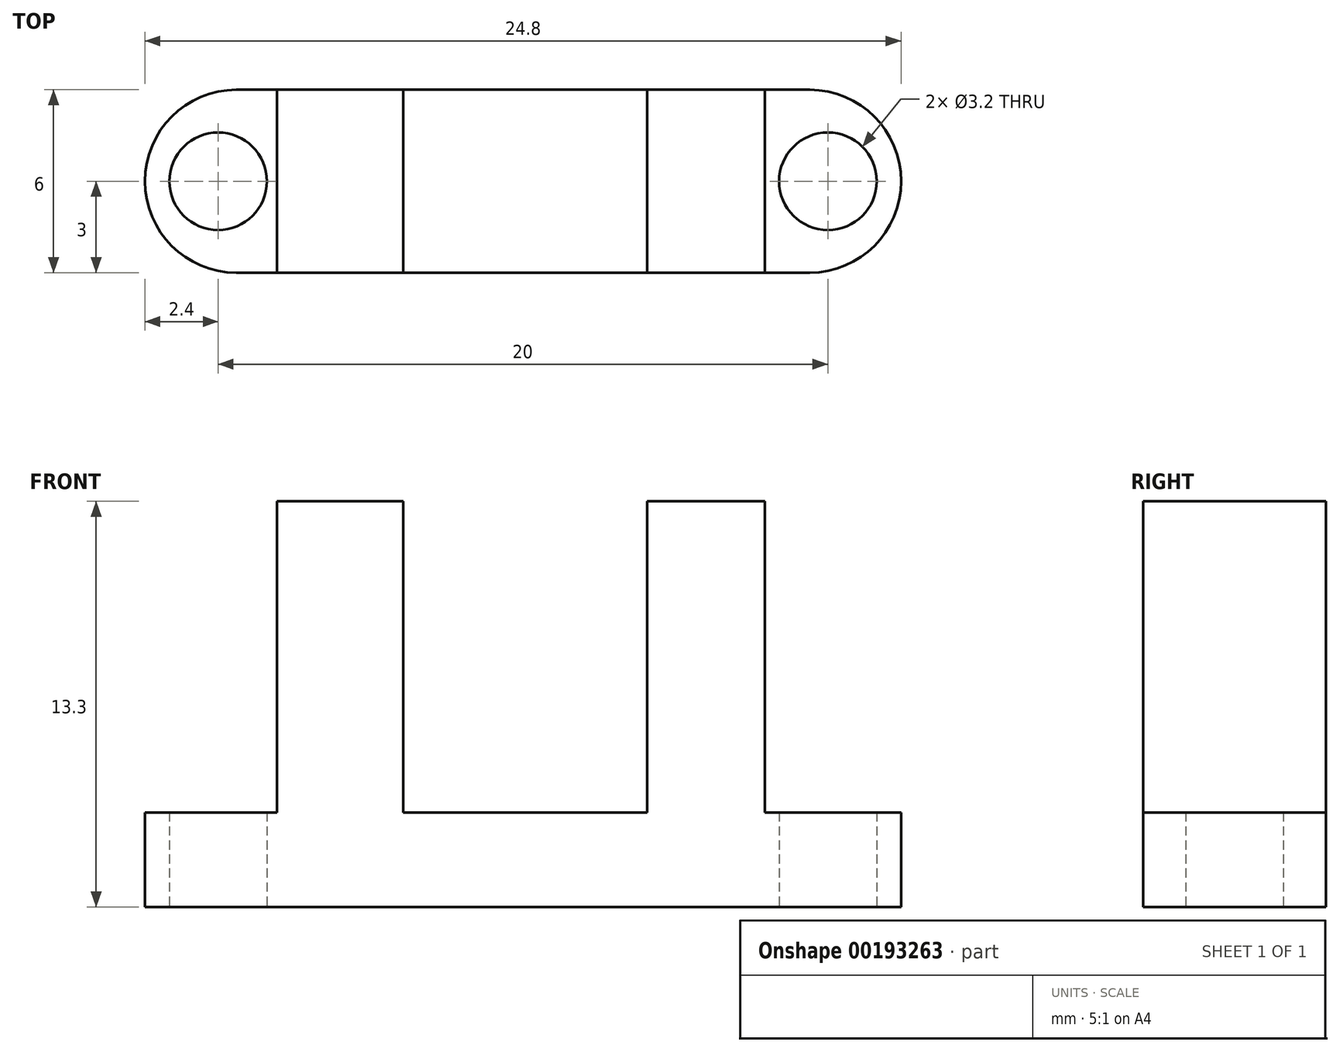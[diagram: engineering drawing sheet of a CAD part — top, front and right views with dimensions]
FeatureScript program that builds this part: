
annotation { "Feature Type Name" : "Feature", "Feature Type Description" : "" }
export const myFeature = defineFeature(function(context is Context, id is Id, definition is map)
    precondition{}
    {
        {
            var Q0;
            Q0=qCreatedBy(makeId("Top.planeOp"),FACE);
            var sketch = newSketch(context, id + "F0", { "sketchPlane" : qUnion([Q0])});
            skLineSegment(sketch, "E0.bottom", {"start": v(9.4, 3) * mm, "end": v(-9.4, 3) * mm});
            skLineSegment(sketch, "E0.top", {"start": v(9.4, -3) * mm, "end": v(-9.4, -3) * mm});
            skLineSegment(sketch, "E0.left", {"start": v(12.4, 0) * mm, "end": v(12.4, 0) * mm});
            skLineSegment(sketch, "E0.right", {"start": v(-12.4, 0) * mm, "end": v(-12.4, 0) * mm});
            skPoint(sketch, "E0.middle", {"position": v(0, 0) * mm});
            skLineSegment(sketch, "E1", {"start": v(0, 0) * mm, "end": v(10, 0) * mm});
            skCircle(sketch, "E2", {"center": v(10, 0) * mm, "radius": 1.6 * mm});
            skLineSegment(sketch, "E3", {"start": v(0, 0) * mm, "end": v(-10, 0) * mm});
            skCircle(sketch, "E4", {"center": v(-10, 0) * mm, "radius": 1.6 * mm});
            skPoint(sketch, "E5.visualSharp", {"position": v(-12.4, 3) * mm});
            skArc(sketch, "E5.filletArc", {"start": v(-9.4, 3) * mm, "mid": v(-11.52, 2.12) * mm, "end": v(-12.4, 0) * mm});
            skPoint(sketch, "E6.visualSharp", {"position": v(12.4, 3) * mm});
            skArc(sketch, "E6.filletArc", {"start": v(12.4, 0) * mm, "mid": v(11.52, 2.12) * mm, "end": v(9.4, 3) * mm});
            skPoint(sketch, "E7.visualSharp", {"position": v(-12.4, -3) * mm});
            skArc(sketch, "E7.filletArc", {"start": v(-12.4, 0) * mm, "mid": v(-11.52, -2.12) * mm, "end": v(-9.4, -3) * mm});
            skPoint(sketch, "E8.visualSharp", {"position": v(12.4, -3) * mm});
            skArc(sketch, "E8.filletArc", {"start": v(9.4, -3) * mm, "mid": v(11.52, -2.12) * mm, "end": v(12.4, 0) * mm});
            skSolve(sketch);
        }
        {
            var Q0;
            Q0 = qSketchRegion(id + "F0", true);
            extrude(context, id + "F1", {"entities" : qUnion([Q0]), "depth" : 3.1 * mm});
        }
        {
            var Q0;
            Q0=makeQuery(id+"F1.opExtrude","CAP_FACE",FACE,{"disambiguationData":[OSD([sQuery(id+"F0.wireOp",EDGE,"E0.bottom"),sQuery(id+"F0.wireOp",EDGE,"E0.top"),sQuery(id+"F0.wireOp",EDGE,"E0.left"),sQuery(id+"F0.wireOp",EDGE,"E0.right"),sQuery(id+"F0.wireOp",EDGE,"E2"),sQuery(id+"F0.wireOp",EDGE,"E4"),sQuery(id+"F0.wireOp",EDGE,"E5.filletArc"),sQuery(id+"F0.wireOp",EDGE,"E6.filletArc"),sQuery(id+"F0.wireOp",EDGE,"E7.filletArc"),sQuery(id+"F0.wireOp",EDGE,"E8.filletArc")])],"isStart":false});
            var sketch = newSketch(context, id + "F2", { "sketchPlane" : qUnion([Q0])});
            skLineSegment(sketch, "E9", {"start": v(0, 0) * mm, "end": v(6, 0) * mm});
            skLineSegment(sketch, "E10.bottom", {"start": v(7.93, 3) * mm, "end": v(4.07, 3) * mm});
            skLineSegment(sketch, "E10.top", {"start": v(7.93, -3) * mm, "end": v(4.07, -3) * mm});
            skLineSegment(sketch, "E10.left", {"start": v(7.93, 3) * mm, "end": v(7.93, -3) * mm});
            skLineSegment(sketch, "E10.right", {"start": v(4.07, 3) * mm, "end": v(4.07, -3) * mm});
            skPoint(sketch, "E10.middle", {"position": v(6, 0) * mm});
            skLineSegment(sketch, "E11", {"start": v(0, 0) * mm, "end": v(-6, 0) * mm});
            skLineSegment(sketch, "E12.bottom", {"start": v(-3.93, 3) * mm, "end": v(-8.07, 3) * mm});
            skLineSegment(sketch, "E12.top", {"start": v(-3.93, -3) * mm, "end": v(-8.07, -3) * mm});
            skLineSegment(sketch, "E12.left", {"start": v(-3.93, 3) * mm, "end": v(-3.93, -3) * mm});
            skLineSegment(sketch, "E12.right", {"start": v(-8.07, 3) * mm, "end": v(-8.07, -3) * mm});
            skPoint(sketch, "E12.middle", {"position": v(-6, 0) * mm});
            skSolve(sketch);
        }
        {
            var Q0;
            {var subQ3=sQuery(id+"F2.wireOp",EDGE,"E12.bottom");Q0=makeQuery(id+"F2.imprint","IMPRINT",FACE,{"disambiguationData":[TD([[makeQuery(id+"F2.imprint","IMPRINT",EDGE,{"derivedFrom":subQ3}),1.0]])]});}
            var Q1;
            {var subQ1=sQuery(id+"F2.wireOp",EDGE,"E10.bottom");Q1=makeQuery(id+"F2.imprint","IMPRINT",FACE,{"disambiguationData":[TD([[makeQuery(id+"F2.imprint","IMPRINT",EDGE,{"derivedFrom":subQ1}),1.0]])]});}
            extrude(context, id + "F3", {"entities" : qUnion([Q0, Q1]), "operationType" : NewBodyOperationType.ADD, "depth" : 10.2 * mm});
        }
    });
